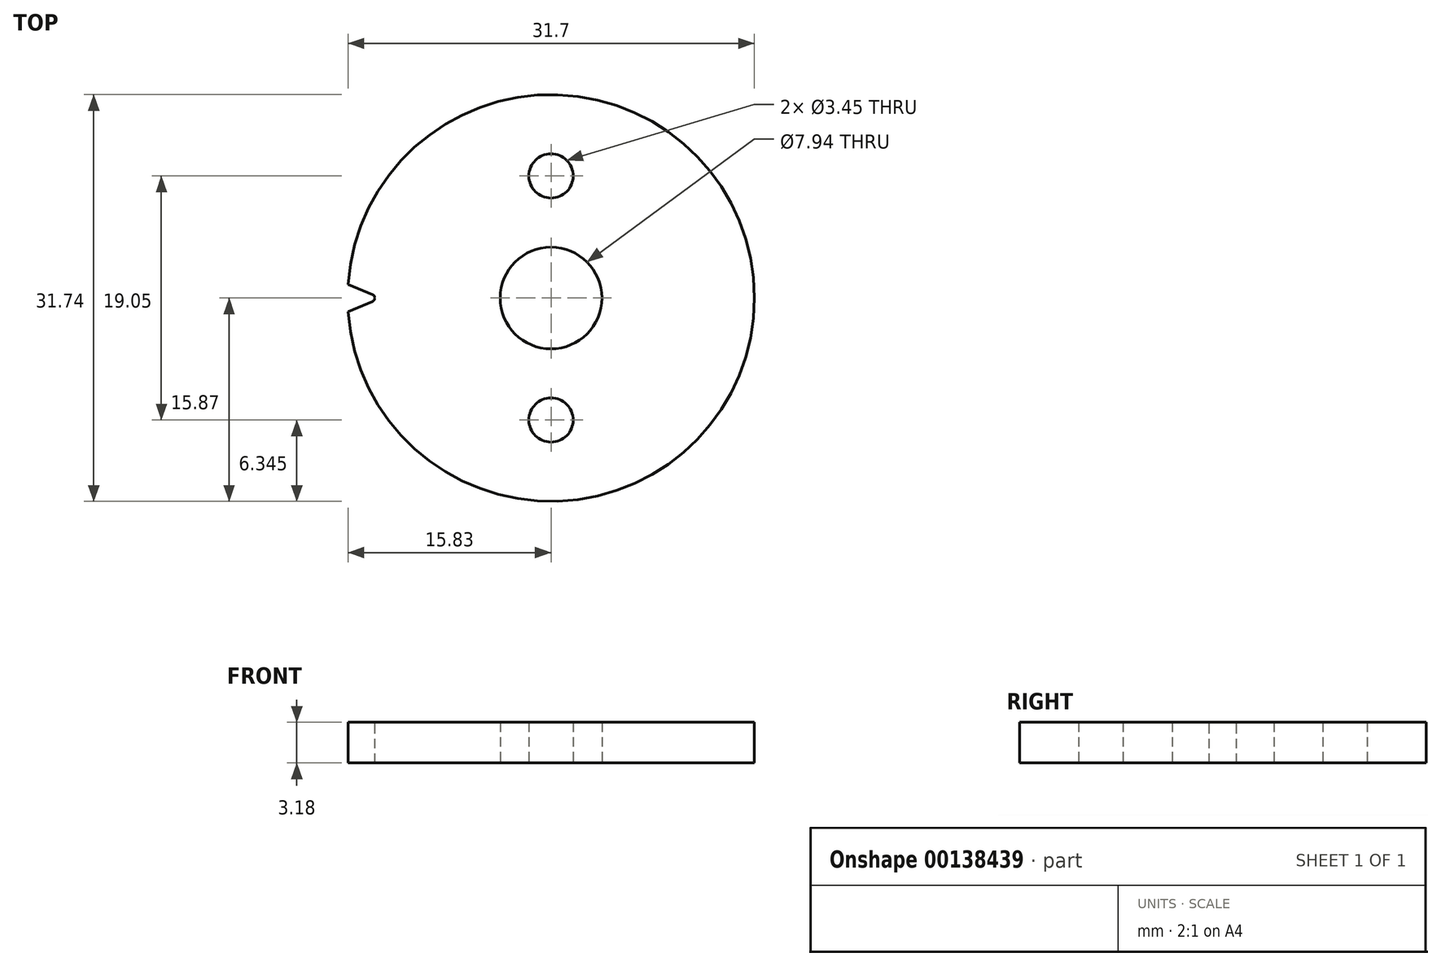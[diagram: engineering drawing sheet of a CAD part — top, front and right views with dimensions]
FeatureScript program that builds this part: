
annotation { "Feature Type Name" : "Feature", "Feature Type Description" : "" }
export const myFeature = defineFeature(function(context is Context, id is Id, definition is map)
    precondition{}
    {
        {
            var Q0;
            Q0=qCreatedBy(makeId("Top.planeOp"),FACE);
            var sketch = newSketch(context, id + "F0", { "sketchPlane" : qUnion([Q0])});
            skCircle(sketch, "E0", {"center": v(0, 0) * mm, "radius": 15.87 * mm});
            skLineSegment(sketch, "E1", {"start": v(0, 9.53) * mm, "end": v(0, -9.53) * mm, "construction": true});
            skCircle(sketch, "E2", {"center": v(0, 0) * mm, "radius": 3.97 * mm});
            skCircle(sketch, "E3", {"center": v(0, 9.53) * mm, "radius": 1.73 * mm});
            skCircle(sketch, "E4", {"center": v(0, -9.53) * mm, "radius": 1.73 * mm});
            skSolve(sketch);
        }
        {
            var Q0;
            Q0=qSketchRegion(id+"F0",true);
            extrude(context, id + "F1", {"entities" : qUnion([Q0]), "depth" : 3.17 * mm});
        }
        {
            var Q0;
            Q0=makeQuery(id+"F1.opExtrude","CAP_FACE",FACE,{"disambiguationData":[OSD([sQuery(id+"F0.wireOp",EDGE,"E0"),sQuery(id+"F0.wireOp",EDGE,"E2"),sQuery(id+"F0.wireOp",EDGE,"E3"),sQuery(id+"F0.wireOp",EDGE,"E4")])],"isStart":false});
            var sketch = newSketch(context, id + "F2", { "sketchPlane" : qUnion([Q0])});
            skLineSegment(sketch, "E5", {"start": v(0, 0) * mm, "end": v(-15.87, 0) * mm, "construction": true});
            skLineSegment(sketch, "E6", {"start": v(0, 0) * mm, "end": v(-15.85, 0.71) * mm, "construction": true});
            skArc(sketch, "E7", {"start": v(-15.83, 1.07) * mm, "mid": v(-15.87, 0) * mm, "end": v(-15.83, -1.07) * mm});
            skArc(sketch, "E8", {"start": v(-13.93, -0.27) * mm, "mid": v(-13.75, 0) * mm, "end": v(-13.93, 0.27) * mm});
            skLineSegment(sketch, "E9", {"start": v(-15.83, -1.07) * mm, "end": v(-13.93, -0.27) * mm});
            skLineSegment(sketch, "E10", {"start": v(-13.93, 0.27) * mm, "end": v(-15.83, 1.07) * mm});
            skPoint(sketch, "E11", {"position": v(-14.88, 0.67) * mm});
            skSolve(sketch);
        }
        {
            var Q0;
            Q0 = qSketchRegion(id + "F2", true);
            var Q1;
            Q1=makeQuery(id+"F1.opExtrude","CAP_FACE",FACE,{"disambiguationData":[OSD([sQuery(id+"F0.wireOp",EDGE,"E0"),sQuery(id+"F0.wireOp",EDGE,"E2"),sQuery(id+"F0.wireOp",EDGE,"E3"),sQuery(id+"F0.wireOp",EDGE,"E4")])],"isStart":true});
            extrude(context, id + "F3", {"entities" : qUnion([Q0]), "operationType" : NewBodyOperationType.REMOVE, "endBound" : BoundingType.UP_TO_SURFACE, "oppositeDirection" : true, "endBoundEntityFace" : qUnion([Q1]), "depth" : 25.4 * mm});
        }
    });
